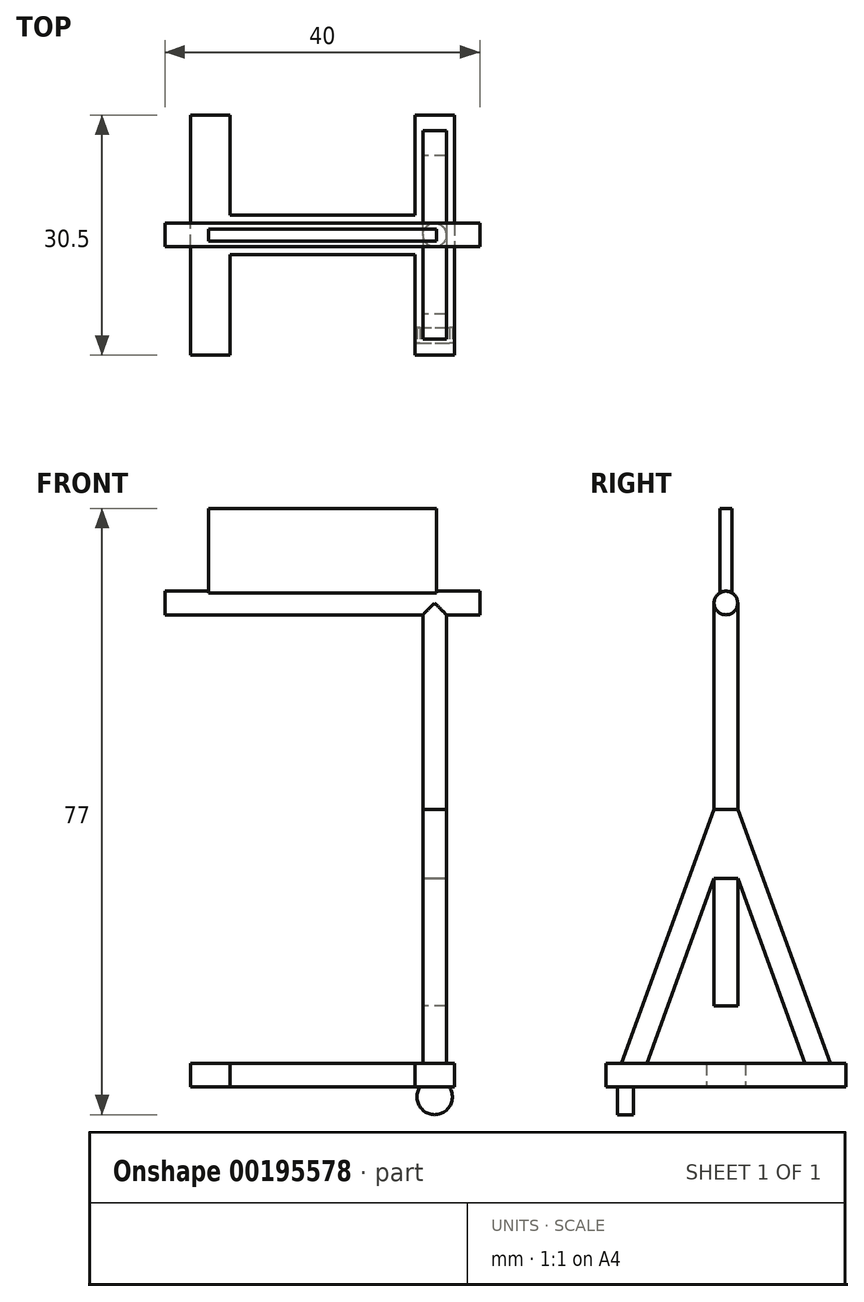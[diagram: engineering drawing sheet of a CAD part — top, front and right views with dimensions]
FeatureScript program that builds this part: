
annotation { "Feature Type Name" : "Feature", "Feature Type Description" : "" }
export const myFeature = defineFeature(function(context is Context, id is Id, definition is map)
    precondition{}
    {
        {
            var Q0;
            Q0=qCreatedBy(makeId("Top.planeOp"),FACE);
            cPlane(context, id + "F0", {"entities" : qUnion([Q0]), "cplaneType" : CPlaneType.OFFSET, "offset" : (70 / 20) * mm, "width" : 150 * mm, "height" : 150 * mm});
        }
        {
            var Q0;
            Q0=qCreatedBy(id+"F0.planeOp",FACE);
            var sketch = newSketch(context, id + "F1", { "sketchPlane" : qUnion([Q0])});
            skLineSegment(sketch, "E0", {"start": v(16.75, 0) * mm, "end": v(16.75, -15.25) * mm});
            skLineSegment(sketch, "E1", {"start": v(16.75, -15.25) * mm, "end": v(11.75, -15.25) * mm});
            skLineSegment(sketch, "E2", {"start": v(11.75, -15.25) * mm, "end": v(11.75, 2.5) * mm});
            skLineSegment(sketch, "E3", {"start": v(11.75, 2.5) * mm, "end": v(0, 2.5) * mm});
            skLineSegment(sketch, "E4.MirrorCS", {"start": v(16.75, 0) * mm, "end": v(16.75, 15.25) * mm});
            skLineSegment(sketch, "E5.MirrorCS", {"start": v(11.75, 15.25) * mm, "end": v(11.75, -2.5) * mm});
            skLineSegment(sketch, "E6.MirrorCS", {"start": v(11.75, -2.5) * mm, "end": v(0, -2.5) * mm});
            skLineSegment(sketch, "E7.MirrorCS", {"start": v(16.75, 15.25) * mm, "end": v(11.75, 15.25) * mm});
            skLineSegment(sketch, "E8.MirrorCS", {"start": v(-11.75, -2.5) * mm, "end": v(0, -2.5) * mm});
            skLineSegment(sketch, "E9.MirrorCS", {"start": v(-11.75, 15.25) * mm, "end": v(-11.75, -2.5) * mm});
            skLineSegment(sketch, "E10.MirrorCS", {"start": v(-16.75, 0) * mm, "end": v(-16.75, 15.25) * mm});
            skLineSegment(sketch, "E11.MirrorCS", {"start": v(-11.75, 2.5) * mm, "end": v(0, 2.5) * mm});
            skLineSegment(sketch, "E12.MirrorCS", {"start": v(-11.75, -15.25) * mm, "end": v(-11.75, 2.5) * mm});
            skLineSegment(sketch, "E13.MirrorCS", {"start": v(-16.75, -15.25) * mm, "end": v(-11.75, -15.25) * mm});
            skLineSegment(sketch, "E14.MirrorCS", {"start": v(-16.75, 0) * mm, "end": v(-16.75, -15.25) * mm});
            skLineSegment(sketch, "E15.MirrorCS", {"start": v(-16.75, 15.25) * mm, "end": v(-11.75, 15.25) * mm});
            skSolve(sketch);
        }
        {
            var Q0;
            {var subQ2=sQuery(id+"F1.wireOp",EDGE,"E9.MirrorCS");Q0=makeQuery(id+"F1.imprint","IMPRINT",FACE,{"disambiguationData":[TD([[makeQuery(id+"F1.imprint","IMPRINT",EDGE,{"derivedFrom":subQ2}),-1.0]])]});}
            var Q1;
            {var subQ3=sQuery(id+"F1.wireOp",EDGE,"E3");Q1=makeQuery(id+"F1.imprint","IMPRINT",FACE,{"disambiguationData":[TD([[makeQuery(id+"F1.imprint","IMPRINT",EDGE,{"derivedFrom":subQ3}),1.0]])]});}
            var Q2;
            Q2=makeQuery(id+"F1.imprint","IMPRINT",FACE,{"disambiguationData":[TD([[makeQuery(id+"F1.imprint","IMPRINT",EDGE,{"derivedFrom":sQuery(id+"F1.wireOp",EDGE,"E0")}),-1.0]])]});
            extrude(context, id + "F2", {"entities" : qUnion([Q0, Q1, Q2]), "depth" : ((40 / 20) + 1) * mm});
        }
        {
            var Q0;
            Q0=makeQuery(id+"F2.opExtrude","CAP_EDGE",EDGE,{"disambiguationData":[OSD([sQuery(id+"F1.wireOp",EDGE,"E1")])],"isStart":false});
            cPoint(context, id + "F3", {"entities" : qUnion([Q0]), "parameter" : 0.5});
        }
        {
            var Q0;
            Q0=qCreatedBy(id+"F3",VERTEX);
            var Q1;
            Q1=qCreatedBy(makeId("Right.planeOp"),FACE);
            cPlane(context, id + "F4", {"entities" : qUnion([Q0, Q1]), "cplaneType" : CPlaneType.PLANE_POINT, "offset" : 25 * mm, "width" : 150 * mm, "height" : 150 * mm});
        }
        {
            var Q0;
            Q0=qCreatedBy(id+"F4.planeOp",FACE);
            var sketch = newSketch(context, id + "F5", { "sketchPlane" : qUnion([Q0])});
            skLineSegment(sketch, "E16", {"start": v(13.25, 6.5) * mm, "end": v(1.5, 38.8) * mm});
            skLineSegment(sketch, "E17", {"start": v(0, 0) * mm, "end": v(0, 26.28) * mm, "construction": true});
            skLineSegment(sketch, "E18", {"start": v(10.06, 6.5) * mm, "end": v(1.5, 30.02) * mm});
            skLineSegment(sketch, "E19", {"start": v(1.5, 30.02) * mm, "end": v(0, 30.02) * mm});
            skLineSegment(sketch, "E20", {"start": v(1.5, 38.8) * mm, "end": v(0, 38.8) * mm});
            skLineSegment(sketch, "E21", {"start": v(10.06, 6.5) * mm, "end": v(13.25, 6.5) * mm});
            skLineSegment(sketch, "E22.MirrorCS", {"start": v(-1.5, 38.8) * mm, "end": v(0, 38.8) * mm});
            skLineSegment(sketch, "E23.MirrorCS", {"start": v(-1.5, 30.02) * mm, "end": v(0, 30.02) * mm});
            skLineSegment(sketch, "E24.MirrorCS", {"start": v(-10.06, 6.5) * mm, "end": v(-13.25, 6.5) * mm});
            skLineSegment(sketch, "E25.MirrorCS", {"start": v(-10.06, 6.5) * mm, "end": v(-1.5, 30.02) * mm});
            skLineSegment(sketch, "E26.MirrorCS", {"start": v(-13.25, 6.5) * mm, "end": v(-1.5, 38.8) * mm});
            skSolve(sketch);
        }
        {
            var Q0;
            Q0=makeQuery(id+"F5.imprint","IMPRINT",FACE,{"disambiguationData":[TD([[makeQuery(id+"F5.imprint","IMPRINT",EDGE,{"derivedFrom":sQuery(id+"F5.wireOp",EDGE,"E16")}),1.0]])]});
            extrude(context, id + "F6", {"entities" : qUnion([Q0]), "operationType" : NewBodyOperationType.ADD, "endBound" : BoundingType.SYMMETRIC, "depth" : ((40 / 20) + 1) * mm});
        }
        {
            var Q0;
            Q0=qCreatedBy(makeId("Top.planeOp"),FACE);
            cPlane(context, id + "F7", {"entities" : qUnion([Q0]), "cplaneType" : CPlaneType.OFFSET, "offset" : 65 * mm, "width" : 150 * mm, "height" : 150 * mm});
        }
        {
            var Q0;
            Q0=makeQuery(id+"F6.opExtrude","SWEPT_FACE",FACE,{"disambiguationData":[OSD([sQuery(id+"F5.wireOp",EDGE,"E20"),sQuery(id+"F5.wireOp",EDGE,"E22.MirrorCS")])]});
            var sketch = newSketch(context, id + "F8", { "sketchPlane" : qUnion([Q0])});
            skCircle(sketch, "E27", {"center": v(14.25, 0) * mm, "radius": 1.5 * mm});
            skPoint(sketch, "E27.centerSnap0", {"position": v(14.25, 1.5) * mm});
            skPoint(sketch, "E27.centerSnap1", {"position": v(15.75, 0) * mm});
            skSolve(sketch);
        }
        {
            var Q0;
            {var subQ0=sQuery(id+"F8.wireOp",EDGE,"E27");var subQ1=sQuery(id+"F5.wireOp",EDGE,"E20");var subQ2=makeQuery(id+"F8.imprint","INTERSECT",VERTEX,{"derivedFrom":[makeQuery(id+"F6.opExtrude","SWEPT_EDGE",EDGE,{"disambiguationData":[OSD([sQuery(id+"F5.wireOp",EDGE,"E16"),subQ1])]}),subQ0]});Q0=makeQuery(id+"F8.imprint","IMPRINT",FACE,{"disambiguationData":[TD([[makeQuery(id+"F8.imprint","IMPRINT",EDGE,{"disambiguationData":[TD([[subQ2,1.0]])],"derivedFrom":subQ0}),1.0]])]});}
            var Q1;
            Q1=qCreatedBy(id+"F7.planeOp",FACE);
            extrude(context, id + "F9", {"entities" : qUnion([Q0]), "operationType" : NewBodyOperationType.ADD, "endBound" : BoundingType.UP_TO_SURFACE, "endBoundEntityFace" : qUnion([Q1]), "depth" : (375 / 20) * mm, "hasSecondDirection" : true, "secondDirectionOppositeDirection" : true, "secondDirectionDepth" : 25 * mm});
        }
        {
            var Q0;
            Q0=qCreatedBy(makeId("Right.planeOp"),FACE);
            var sketch = newSketch(context, id + "F10", { "sketchPlane" : qUnion([Q0])});
            skCircle(sketch, "E28", {"center": v(0, 65) * mm, "radius": 1.5 * mm});
            skLineSegment(sketch, "E29.0.0", {"start": v(-1.5, 65) * mm, "end": v(1.5, 65) * mm, "construction": true});
            skSolve(sketch);
        }
        {
            var Q0;
            Q0=makeQuery(id+"F10.imprint","IMPRINT",FACE,{"disambiguationData":[TD([[makeQuery(id+"F10.imprint","IMPRINT",EDGE,{"derivedFrom":sQuery(id+"F10.wireOp",EDGE,"E28")}),1.0]])]});
            extrude(context, id + "F11", {"entities" : qUnion([Q0]), "operationType" : NewBodyOperationType.ADD, "endBound" : BoundingType.SYMMETRIC, "depth" : (800 / 20) * mm});
        }
        {
            var Q0;
            Q0=makeQuery(id+"F2.opExtrude","SWEPT_FACE",FACE,{"disambiguationData":[OSD([sQuery(id+"F1.wireOp",EDGE,"E1")])]});
            cPlane(context, id + "F12", {"entities" : qUnion([Q0]), "cplaneType" : CPlaneType.OFFSET, "offset" : 1.5 * mm, "oppositeDirection" : true, "width" : 150 * mm, "height" : 150 * mm});
        }
        {
            var Q0;
            Q0=qCreatedBy(id+"F12.planeOp",FACE);
            var sketch = newSketch(context, id + "F13", { "sketchPlane" : qUnion([Q0])});
            skCircle(sketch, "E30", {"center": v(14.25, 2.25) * mm, "radius": 2.25 * mm});
            skSolve(sketch);
        }
        {
            var Q0;
            Q0=makeQuery(id+"F13.imprint","IMPRINT",FACE,{"disambiguationData":[TD([[makeQuery(id+"F13.imprint","IMPRINT",EDGE,{"derivedFrom":sQuery(id+"F13.wireOp",EDGE,"E30")}),1.0]])]});
            extrude(context, id + "F14", {"entities" : qUnion([Q0]), "operationType" : NewBodyOperationType.ADD, "oppositeDirection" : true, "depth" : 2 * mm});
        }
        {
            var Q0;
            Q0=qCreatedBy(makeId("Front.planeOp"),FACE);
            var sketch = newSketch(context, id + "F15", { "sketchPlane" : qUnion([Q0])});
            skLineSegment(sketch, "E31.bottom", {"start": v(14.5, 66) * mm, "end": v(-14.5, 66) * mm});
            skLineSegment(sketch, "E31.top", {"start": v(14.5, 77) * mm, "end": v(-14.5, 77) * mm});
            skLineSegment(sketch, "E31.left", {"start": v(14.5, 66) * mm, "end": v(14.5, 77) * mm});
            skLineSegment(sketch, "E31.right", {"start": v(-14.5, 66) * mm, "end": v(-14.5, 77) * mm});
            skPoint(sketch, "E31.middle", {"position": v(0, 71.5) * mm});
            skLineSegment(sketch, "E32.0", {"start": v(20, 66.5) * mm, "end": v(20, 63.5) * mm, "construction": true});
            skSolve(sketch);
        }
        {
            var Q0;
            Q0=makeQuery(id+"F15.imprint","IMPRINT",FACE,{"disambiguationData":[TD([[makeQuery(id+"F15.imprint","IMPRINT",EDGE,{"derivedFrom":sQuery(id+"F15.wireOp",EDGE,"E31.bottom")}),-1.0]])]});
            extrude(context, id + "F16", {"entities" : qUnion([Q0]), "operationType" : NewBodyOperationType.ADD, "endBound" : BoundingType.SYMMETRIC, "depth" : 1.5 * mm});
        }
    });
